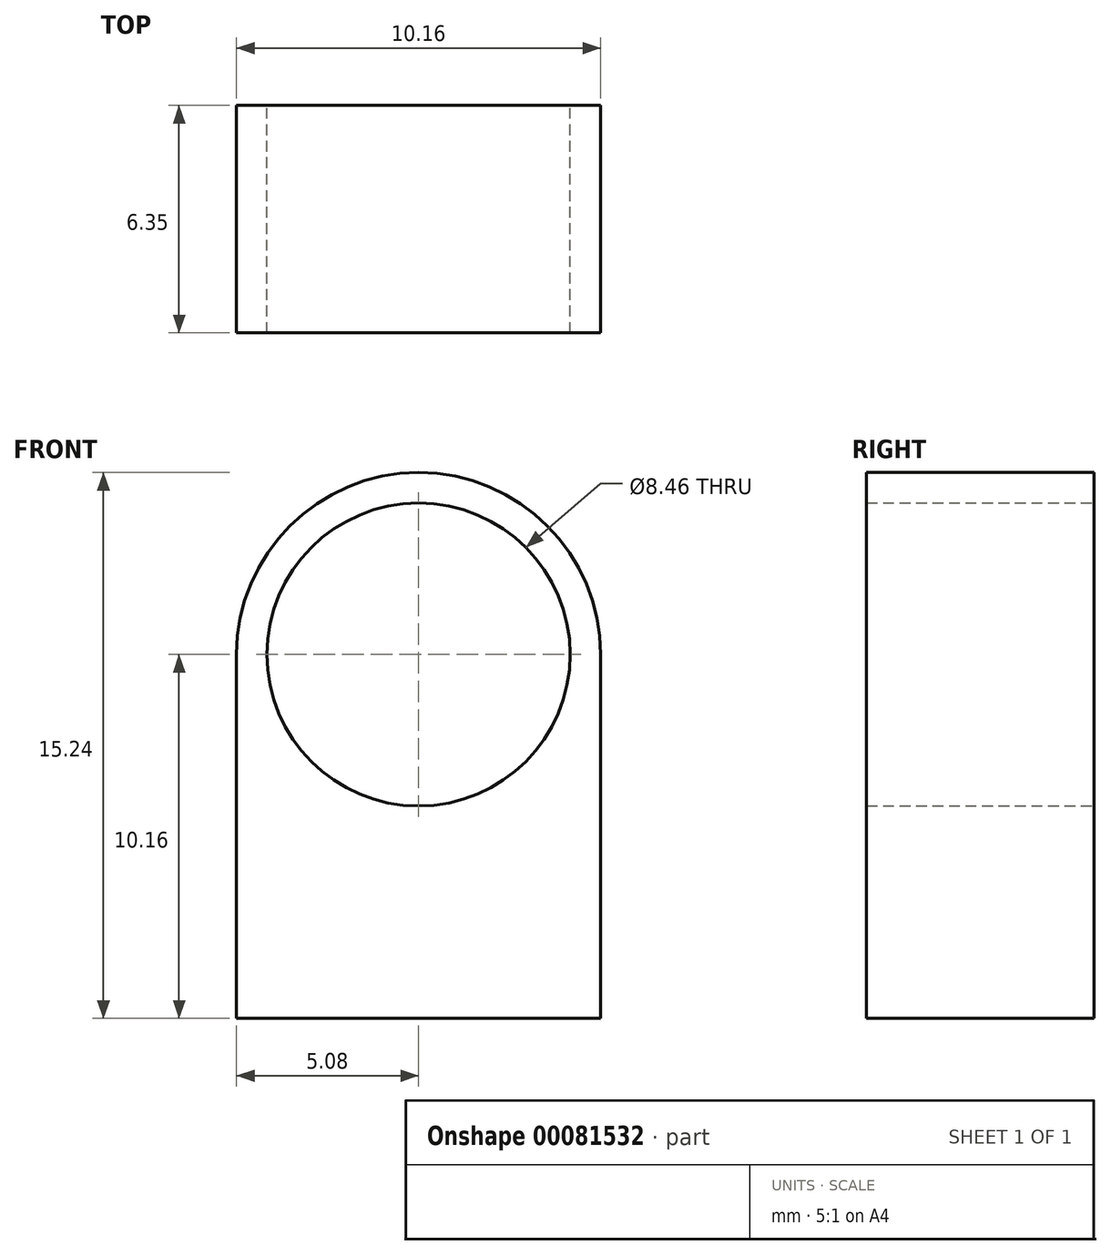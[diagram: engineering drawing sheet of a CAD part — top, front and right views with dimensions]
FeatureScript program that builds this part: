
annotation { "Feature Type Name" : "Feature", "Feature Type Description" : "" }
export const myFeature = defineFeature(function(context is Context, id is Id, definition is map)
    precondition{}
    {
        {
            var Q0;
            Q0=qCreatedBy(makeId("Front.planeOp"),FACE);
            var sketch = newSketch(context, id + "F0", { "sketchPlane" : qUnion([Q0])});
            skLineSegment(sketch, "E0.bottom", {"start": v(5.08, -5.08) * mm, "end": v(-5.08, -5.08) * mm});
            skLineSegment(sketch, "E0.right", {"start": v(-5.08, -5.08) * mm, "end": v(-5.08, 5.08) * mm});
            skPoint(sketch, "E0.middle", {"position": v(0, 0) * mm});
            skLineSegment(sketch, "E1", {"start": v(5.08, 5.08) * mm, "end": v(5.08, -5.08) * mm});
            skPoint(sketch, "E2.orphan", {"position": v(0, -5.08) * mm});
            skPoint(sketch, "E3.start.orphan", {"position": v(0, 5.08) * mm});
            skArc(sketch, "E4", {"start": v(5.08, 5.08) * mm, "mid": v(0, 10.16) * mm, "end": v(-5.08, 5.08) * mm});
            skCircle(sketch, "E5", {"center": v(0, 5.08) * mm, "radius": 4.23 * mm});
            skSolve(sketch);
        }
        {
            var Q0;
            Q0 = qSketchRegion(id + "F0", true);
            extrude(context, id + "F1", {"entities" : qUnion([Q0]), "depth" : 6.35 * mm});
        }
    });
